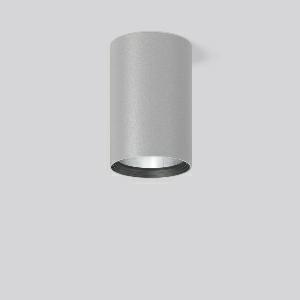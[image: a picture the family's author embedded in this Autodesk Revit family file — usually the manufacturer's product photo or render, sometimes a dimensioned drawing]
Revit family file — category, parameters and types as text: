
# Revit family: heledon_maxi_a_931226_004_1_eb96
name_source: partatom
category: Lighting Fixtures
units: mm (PartAtom-declared; Revit-internal decimal feet)

## family parameters
Cut with Voids When Loaded = No
Host = Face
Light Source = No
Part Type = Normal
Room Calculation Point = No
Round Connector Dimension = Use Diameter
Shared = No

## types (1)
- HELEDON maxi A (1 x LED Modul 940, 4400 lm, 4000)
    Apparent Load = 35 VA
    Approval mark = CE
    CIE Flux Codes = 97 100 100 100 100
    Color Rendering = 92
    Color Temperature = 4000
    Default Elevation = 1800 mm
    Description = Series: HELEDON maxi
Cylindrical surface-mounted downlight. Housing: die-cast aluminium, powder-coated. Internal ceiling frame polycarbonate with bayonet mounting. Black plastic ring and recessed LED to prevent glare from the side. Optical assembly with reflector made of MIRO-Silver with 98% total light reflection for outstanding efficiency - can be changed without tools. Best colour rendering index Ra>90. Suitable for Ceiling mounting. Easy installation with a separate ceiling frame with bayonet mounting and plug connection. Driver integrated. Connected via plug-in connector. High quality converter without flickering and stroboscopic effect. The following accessories can be mounted without use of tools: interchangeable lenses, decorative glasses, honeycomb louvre, clear and frosted diffusers, white interchangeable plastic ring. 
Colour: silver
Diameter: 123 mm
Height: 183 mm
Lamp: LED
Socket: without socket
Colour temperature: 4000K
Colour rendering index (CRI): 92
System power: 35 W
Rated luminous flux: 4400 lm
Luminous efficiency: 126 lm/W
Control gear: Regulated power supply
Protection class: I
Type of protection: IP 20
    Height = 183 mm
    Lamp = 1 x LED Modul 940
    Lamp Light Flux = 4400 lm
    Lamp count = 1
    Length = 123 mm
    Lifetime = 50000 h
    Luminous efficacy = 126 lm/W
    Manufacturer = RZB
    ModVariant = No
    Model = 931226.004.1
    Mounting Place = Ceiling
    Mounting Type = Surface mounted
    Number of Poles = 1
    OnlyDefault = Yes
    Power Factor = 1
    Product Name = HELEDON maxi A
    Product group = Surface mounted downlights
    ProductGroupID = 302
    Protection Class = Protection class I
    Protection Degree = IP 20
    RLX_Detail_Level = 1
    RLX_Emergency_Light_Flux = 0 lm
    RLX_Emergency_Type = 0
    RLX_Emergency_Type_DB = No
    RlxData = <blob elided: 98717 chars, md5=4222b59f>
    Socket = socket
    Standby Power = 0 W
    System Light Flux = 4400 lm
    System Power = 35 W
    Type Comments = Product without accessories
    Type Image = 931192.004.jpg
    URL = http://relux.com
    VarID = ---
    Voltage = 230 V
    Voltage Range = 220-240 V
    Weight = 0.00 kg
    Width = 0 mm  [stored 0 ft]

note: [stored X ft] marks values corroborated as IEEE doubles in the binary element streams (Revit-internal decimal feet)

## geometry (parser evidence)
native form markers: Blend x4, Sweep x10
no freeform markers — native parametric forms only
